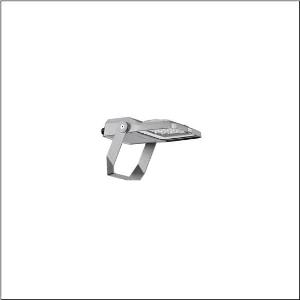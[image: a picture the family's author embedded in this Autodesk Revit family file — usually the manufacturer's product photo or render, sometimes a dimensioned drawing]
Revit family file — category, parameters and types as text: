
# Revit family: floodlight_fl_21_iq_micro___rs12_5xa7761a4b1a_38e5
name_source: partatom
category: Lighting Fixtures
units: mm (PartAtom-declared; Revit-internal decimal feet)

## family parameters
Cut with Voids When Loaded = No
Host = Face
Light Source = No
Part Type = Normal
Room Calculation Point = No
Round Connector Dimension = Use Diameter
Shared = No

## types (1)
- --- (1 x LED, 3220 lm, 23.1 W, 4000K)
    Apparent Load = 23 VA
    CIE Flux Codes = 79 92 99 100 100
    Color Rendering = 70
    Color Temperature = 4000K
    Default Elevation = 1800 mm
    Description = Floodlight FL 21 iQ micro, floodlight, primary light control with lens, of PMMA, primary optical cover: protective disc, of toughened safety glass, transparent, light distribution: RS12, light emission: direct distribution, installation type: surface-mounted, LED, High Power LED, rated luminous flux: 3.220lm, luminous efficacy: 139lm/W, light colour: 740, colour temperature: 4000K, control: optimised constant luminous flux control (CLO 2.0), Desk-Remote (wireless, voltage-free reading and setting of iQ features in the workshop via application-optimized NFC function/RFID function), Light-Fading, Smart-Wire, Night-Set, Lumen-Switch, Temp-Guard, Auto-Match, with terminal, 6-pole, mains connection: 220..240V, AC, 50/60Hz, start of lifetime: 23W, end of service life: 24W, reduction: 11W, luminaire housing, of diecast aluminium, powder-coated, Siteco® metallic grey (DB 702S), corrosivity category C5 mid according to DIN EN ISO 12944, sealing non-destructively replaceable, mounting bracket, of steel, galvanised, powder-coated, Siteco® metallic grey (DB 702S), protection rating (complete): IP66, insulation class (complete): insulation class II (safety insulation), certification: CE, ENEC, VDE, protection symbol: D, impact resistance: IK07, permissible operating ambient temperature: -40..+40°C, permissible operating ambient temperature for outdoor applications: -40..+50°C, standard: DIN EN 12944, LABS conformity tested according to VDMA 24364:2018-05, packaging unit: 1 piece

Light Distribution: RS12
    Height = 65 mm
    Lamp = 1 x LED
    Lamp Light Flux = 3220 lm
    Lamp Power = 23.1 W
    Lamp count = 1
    Length = 312 mm
    Luminous efficacy = 139 lm/W
    Manufacturer = Siteco
    ModVariant = No
    Model = 5XA7761A4B1A
    Mounting Place = Wall
    Mounting Type = Surface mounted
    Number of Poles = 1
    OnlyDefault = Yes
    Power Factor = 1
    Product Name = Floodlight FL 21 iQ micro | RS12
    Product group = floodlight | wall mounted
    ProductGroupID = 2001
    Protection Class = Protection class II
    Protection Degree = IP 66
    RLX_Detail_Level = 1
    RLX_Emergency_Light_Flux = 0 lm
    RLX_Emergency_Type = 0
    RLX_Emergency_Type_DB = No
    RlxData = <blob elided: 74957 chars, md5=c8b96787>
    Socket = socket
    Standby Power = 0 W
    System Light Flux = 3220 lm
    System Power = 23 W
    Type Comments = factory setting: luminous flux: 100 % | dim-lin: 254 | 455 mA
    Type Image = l_1006880.jpg
    URL = http://relux.com
    VarID = @adj_133341
    Voltage = 0 V
    Weight = 0.00 kg
    Width = 230 mm

## geometry (parser evidence)
native form markers: Blend x4, Sweep x12
no freeform markers — native parametric forms only
